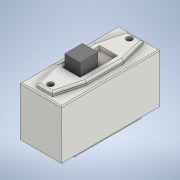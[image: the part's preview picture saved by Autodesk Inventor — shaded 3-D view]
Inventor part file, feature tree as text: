
AUTODESK INVENTOR PART (.ipt)
format: ipt  version: 2022 (Build 260153000, 153)  size: 209,920 bytes
history: native  units: mm
features: sketch x5, extrude x4, fillet x2, chamfer x1
ambient origin geometry x8: Origin, YZ Plane, XZ Plane, XY Plane, X Axis, Y Axis, Z Axis, Center Point
bodies: Solid1 (feature_tree)
feature tree (12):
  sketch  "Sketch1"  dims[d0=10.5mm d1=25.0mm]
  extrude  "Extrusion1"  Depth=25.0mm
  extrude  "Extrusion2"  Depth=12.5mm
  extrude  "Extrusion3"  Depth=4.5mm
  extrude  "Extrusion4"  Depth=9.5mm
  chamfer  "Chamfer1"  Distance=1.5mm
  fillet  "Fillet1"  Radius=1.5mm
  fillet  "Fillet2"  Radius=1.5mm
  sketch  "Sketch2"  dims[d2=12.5mm d3=5.25mm]
  sketch  "Sketch3"  dims[d4=12.5mm d5=0.0mm d6=4.5mm]
  sketch  "Sketch4"  dims[d7=9.5mm d8=4.75mm]
  sketch  "Sketch5"  dims[d9=2.25mm d10=1.5mm d11=1.5mm d12=1.5mm d13=1.5mm d14=2.5mm d15=2.5mm d16=4.0mm d17=3.0mm d18=4.0mm d19=3.0mm d20=1.5mm d21=2.0mm d22=2.0mm d23=1.5mm d24=1.0mm d25=0.0mm d26=0.3mm d27=0.3mm d28=0.3mm d29=4.5mm d30=4.0mm d31=0.0mm d32=9.0mm d33=17.0mm d34=8.5mm d35=4.5mm d36=2.0mm d37=0.0mm d38=1.0mm d39=2.0mm d40=45.0deg d41=0.5mm d42=0.25mm]
